# Revit family: DFM Doors - one leaf door EI 60
name_source: partatom
category: Doors
revit_build: Autodesk Revit 2017 (Build: 20190507_1515(x64)
units: mm (PartAtom-declared; Revit-internal decimal feet)

## family parameters
Always vertical = Yes
Cut with Voids When Loaded = No
Host = Wall
OmniClass Number = 23.30.10.00
OmniClass Title = Doors
Room Calculation Point = Yes
Shared = No

## types (1)
- 2018x916 internal frame
    Clear opening height = 2018 mm  [stored 6.62073 ft]
    Clear opening height. Limiting dimensions = ok
    Clear opening width = 916 mm
    Clear opening width. Limiting dimensions = ok
    Clear opening width. Remarks regarding escape route = ok
    Corner frame = No
    Embracing frame = No
    Escape doors = No
    Fire Rating = EI 60
    Frame to frame width = 932 mm  [stored 3.05774 ft]
    Function = Interior
    Height = 2085 mm  [stored 6.84055 ft]
    Height of the door leaf = 2037 mm  [stored 6.68307 ft]
    Internal frame = Yes
    Manufacturer = DFM Doors sp. z o. o.
    Material of cut-off for the ventilation grid KWZ = DFM Doors - cut-off for the ventilation grid 1
    Material of cut-off for the ventilation grid NV and ZET = DFM Doors - cut-off for the ventilation grid 2
    Material of door closer = DFM Doors - aluminium
    Material of door frame = DFM Doors - aluminium
    Material of door leaf = DFM Doors - zinc coated steel
    Material of drip cap = DFM Doors - zinc coated steel
    Material of glass = DFM Doors - glazing
    Material of glass framing = DFM Doors - zinc coated steel
    Material of hinges = DFM Doors - stainless steel
    Material of ironmongery = DFM Doors - aluminium
    Material of ventilation grid = DFM Doors - zinc coated steel
    Model = DFM DS 60 - 1
    Offset of drip cap = 0 mm  [stored 0 ft]
    Offset of the door leaf = 59 mm
    Offset of the fitting = 412 mm  [stored 1.35171 ft]
    Rough Height = 2085 mm  [stored 6.84055 ft]
    Rough Width = 1066 mm  [stored 3.49738 ft]
    Thickness = 65 mm  [stored 0.213255 ft]
    Type of frame = 2
    URL = https://www.dfm-europe.eu
    Wall Closure = By host
    Width = 1066 mm  [stored 3.49738 ft]
    Width of door leaf = 988 mm
    Width of door leaf. Remark regarding escape route = ok

note: [stored X ft] marks values corroborated as IEEE doubles in the binary element streams (Revit-internal decimal feet)
